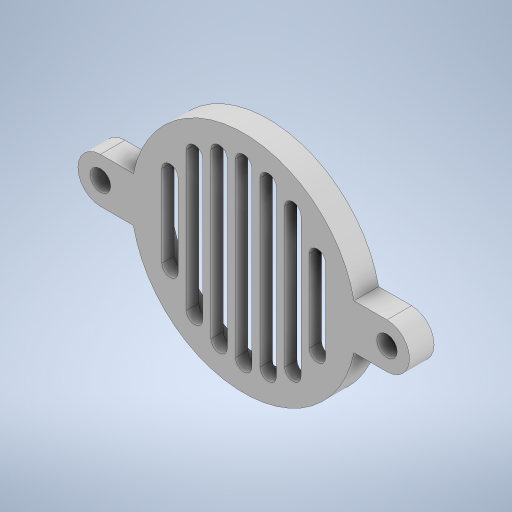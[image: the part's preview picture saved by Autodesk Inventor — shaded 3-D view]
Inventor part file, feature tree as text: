
AUTODESK INVENTOR PART (.ipt)
format: ipt  version: 2023 (Build 270158000, 158)  size: 323,584 bytes
history: native  units: mm
features: extrude x3, sketch x3, other x1
ambient origin geometry x8: Origin, YZ Plane, XZ Plane, XY Plane, X Axis, Y Axis, Z Axis, Center Point
bodies: Body1 (feature_tree)
feature tree (7):
  other  "솔리드1"
  extrude  "돌출1"  Depth=27.5mm
  extrude  "돌출2"  Depth=2.5mm
  extrude  "돌출3"  Depth=5.5mm
  sketch  "스케치1"
  sketch  "스케치2"
  sketch  "스케치3"
